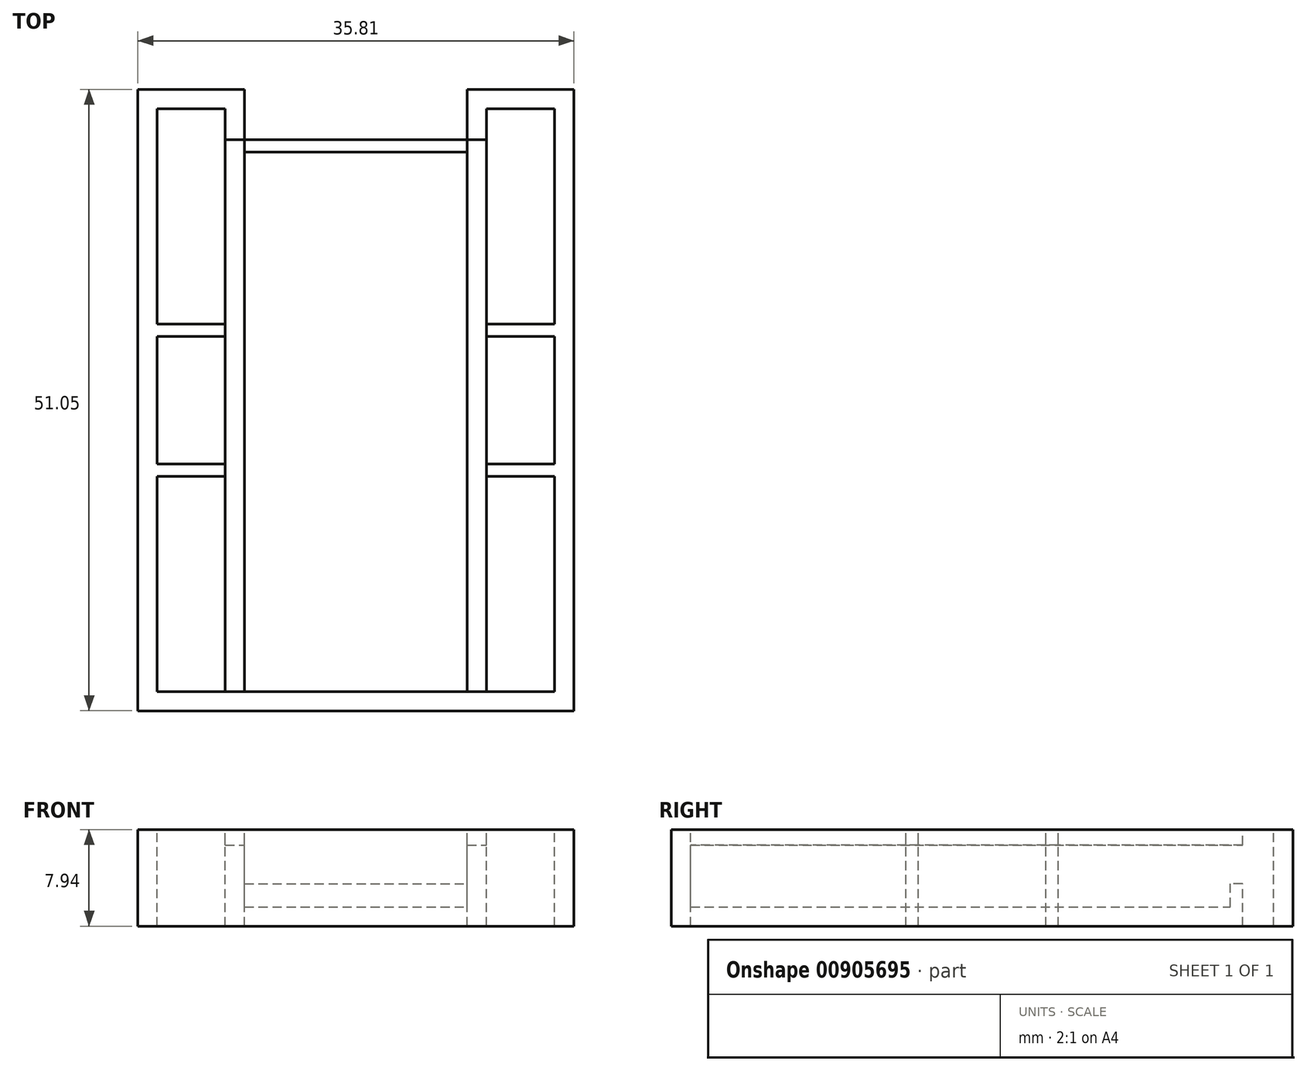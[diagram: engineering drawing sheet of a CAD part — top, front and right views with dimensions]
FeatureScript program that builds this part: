
annotation { "Feature Type Name" : "Feature", "Feature Type Description" : "" }
export const myFeature = defineFeature(function(context is Context, id is Id, definition is map)
    precondition{}
    {
        {
            var Q0;
            Q0=qCreatedBy(makeId("Top.planeOp"),FACE);
            var sketch = newSketch(context, id + "F0", { "sketchPlane" : qUnion([Q0])});
            skLineSegment(sketch, "E0.bottom", {"start": v(-17.05, 33.05) * mm, "end": v(18.76, 33.05) * mm});
            skLineSegment(sketch, "E0.top", {"start": v(-17.05, -18) * mm, "end": v(18.76, -18) * mm});
            skLineSegment(sketch, "E0.left", {"start": v(-17.05, 33.05) * mm, "end": v(-17.05, -18) * mm});
            skLineSegment(sketch, "E0.right", {"start": v(18.76, 33.05) * mm, "end": v(18.76, -18) * mm});
            skSolve(sketch);
        }
        {
            var Q0;
            Q0=makeQuery(id+"F0.imprint","IMPRINT",FACE,{"disambiguationData":[TD([[makeQuery(id+"F0.imprint","IMPRINT",EDGE,{"derivedFrom":sQuery(id+"F0.wireOp",EDGE,"E0.bottom")}),-1.0]])]});
            extrude(context, id + "F1", {"entities" : qUnion([Q0]), "depth" : 7.94 * mm, "offsetDistance" : 25.4 * mm});
        }
        {
            var Q0;
            Q0=makeQuery(id+"F1.opExtrude","CAP_FACE",FACE,{"disambiguationData":[OSD([sQuery(id+"F0.wireOp",EDGE,"E0.bottom"),sQuery(id+"F0.wireOp",EDGE,"E0.top"),sQuery(id+"F0.wireOp",EDGE,"E0.left"),sQuery(id+"F0.wireOp",EDGE,"E0.right")])],"isStart":false});
            var sketch = newSketch(context, id + "F2", { "sketchPlane" : qUnion([Q0])});
            skLineSegment(sketch, "E1.bottom", {"start": v(-15.47, 31.46) * mm, "end": v(-9.88, 31.46) * mm});
            skLineSegment(sketch, "E1.top", {"start": v(-15.47, 13.78) * mm, "end": v(-9.88, 13.78) * mm});
            skLineSegment(sketch, "E1.left", {"start": v(-15.47, 31.46) * mm, "end": v(-15.47, 13.78) * mm});
            skLineSegment(sketch, "E1.right", {"start": v(-9.88, 31.46) * mm, "end": v(-9.88, 13.78) * mm});
            skLineSegment(sketch, "E2.bottom", {"start": v(17.17, 31.46) * mm, "end": v(11.58, 31.46) * mm});
            skLineSegment(sketch, "E2.top", {"start": v(17.17, 13.78) * mm, "end": v(11.58, 13.78) * mm});
            skLineSegment(sketch, "E2.left", {"start": v(17.17, 31.46) * mm, "end": v(17.17, 13.78) * mm});
            skLineSegment(sketch, "E2.right", {"start": v(11.58, 31.46) * mm, "end": v(11.58, 13.78) * mm});
            skLineSegment(sketch, "E3.bottom", {"start": v(-15.47, 1.27) * mm, "end": v(-9.88, 1.27) * mm});
            skLineSegment(sketch, "E3.top", {"start": v(-15.47, -16.42) * mm, "end": v(-9.88, -16.42) * mm});
            skLineSegment(sketch, "E3.left", {"start": v(-15.47, 1.27) * mm, "end": v(-15.47, -16.42) * mm});
            skLineSegment(sketch, "E3.right", {"start": v(-9.88, 1.27) * mm, "end": v(-9.88, -16.42) * mm});
            skLineSegment(sketch, "E4.bottom", {"start": v(11.58, 1.27) * mm, "end": v(17.17, 1.27) * mm});
            skLineSegment(sketch, "E4.top", {"start": v(11.58, -16.42) * mm, "end": v(17.17, -16.42) * mm});
            skLineSegment(sketch, "E4.left", {"start": v(11.58, 1.27) * mm, "end": v(11.58, -16.42) * mm});
            skLineSegment(sketch, "E4.right", {"start": v(17.17, 1.27) * mm, "end": v(17.17, -16.42) * mm});
            skLineSegment(sketch, "E5.bottom", {"start": v(-15.47, 12.76) * mm, "end": v(-9.88, 12.76) * mm});
            skLineSegment(sketch, "E5.top", {"start": v(-15.47, 2.28) * mm, "end": v(-9.88, 2.28) * mm});
            skLineSegment(sketch, "E5.left", {"start": v(-15.47, 12.76) * mm, "end": v(-15.47, 2.28) * mm});
            skLineSegment(sketch, "E5.right", {"start": v(-9.88, 12.76) * mm, "end": v(-9.88, 2.28) * mm});
            skLineSegment(sketch, "E6.bottom", {"start": v(11.58, 12.76) * mm, "end": v(17.17, 12.76) * mm});
            skLineSegment(sketch, "E6.top", {"start": v(11.58, 2.28) * mm, "end": v(17.17, 2.28) * mm});
            skLineSegment(sketch, "E6.left", {"start": v(11.58, 12.76) * mm, "end": v(11.58, 2.28) * mm});
            skLineSegment(sketch, "E6.right", {"start": v(17.17, 12.76) * mm, "end": v(17.17, 2.28) * mm});
            skSolve(sketch);
        }
        {
            var Q0;
            Q0=makeQuery(id+"F2.imprint","IMPRINT",FACE,{"disambiguationData":[TD([[makeQuery(id+"F2.imprint","IMPRINT",EDGE,{"derivedFrom":sQuery(id+"F2.wireOp",EDGE,"E1.bottom")}),-1.0]])]});
            var Q1;
            Q1=makeQuery(id+"F2.imprint","IMPRINT",FACE,{"disambiguationData":[TD([[makeQuery(id+"F2.imprint","IMPRINT",EDGE,{"derivedFrom":sQuery(id+"F2.wireOp",EDGE,"E5.bottom")}),-1.0]])]});
            var Q2;
            Q2=makeQuery(id+"F2.imprint","IMPRINT",FACE,{"disambiguationData":[TD([[makeQuery(id+"F2.imprint","IMPRINT",EDGE,{"derivedFrom":sQuery(id+"F2.wireOp",EDGE,"E3.bottom")}),-1.0]])]});
            var Q3;
            Q3=makeQuery(id+"F2.imprint","IMPRINT",FACE,{"disambiguationData":[TD([[makeQuery(id+"F2.imprint","IMPRINT",EDGE,{"derivedFrom":sQuery(id+"F2.wireOp",EDGE,"E4.bottom")}),-1.0]])]});
            var Q4;
            Q4=makeQuery(id+"F2.imprint","IMPRINT",FACE,{"disambiguationData":[TD([[makeQuery(id+"F2.imprint","IMPRINT",EDGE,{"derivedFrom":sQuery(id+"F2.wireOp",EDGE,"E6.bottom")}),-1.0]])]});
            var Q5;
            Q5=makeQuery(id+"F2.imprint","IMPRINT",FACE,{"disambiguationData":[TD([[makeQuery(id+"F2.imprint","IMPRINT",EDGE,{"derivedFrom":sQuery(id+"F2.wireOp",EDGE,"E2.bottom")}),1.0]])]});
            extrude(context, id + "F3", {"entities" : qUnion([Q0, Q1, Q2, Q3, Q4, Q5]), "operationType" : NewBodyOperationType.REMOVE, "oppositeDirection" : true, "depth" : 25.4 * mm, "offsetDistance" : 25.4 * mm});
        }
        {
            var Q0;
            Q0=makeQuery(id+"F1.opExtrude","CAP_FACE",FACE,{"disambiguationData":[OSD([sQuery(id+"F0.wireOp",EDGE,"E0.bottom"),sQuery(id+"F0.wireOp",EDGE,"E0.top"),sQuery(id+"F0.wireOp",EDGE,"E0.left"),sQuery(id+"F0.wireOp",EDGE,"E0.right")])],"isStart":false});
            var sketch = newSketch(context, id + "F4", { "sketchPlane" : qUnion([Q0])});
            skLineSegment(sketch, "E7.bottom", {"start": v(-9.88, 28.92) * mm, "end": v(11.58, 28.92) * mm});
            skLineSegment(sketch, "E7.top", {"start": v(-9.88, -16.42) * mm, "end": v(11.58, -16.42) * mm});
            skLineSegment(sketch, "E7.left", {"start": v(-9.88, 28.92) * mm, "end": v(-9.88, -16.42) * mm});
            skLineSegment(sketch, "E7.right", {"start": v(11.58, 28.92) * mm, "end": v(11.58, -16.42) * mm});
            skSolve(sketch);
        }
        {
            var Q0;
            {var subQ8=sQuery(id+"F4.wireOp",EDGE,"E7.bottom");Q0=makeQuery(id+"F4.imprint","IMPRINT",FACE,{"disambiguationData":[TD([[makeQuery(id+"F4.imprint","IMPRINT",EDGE,{"derivedFrom":subQ8}),-1.0]])]});}
            extrude(context, id + "F5", {"entities" : qUnion([Q0]), "operationType" : NewBodyOperationType.REMOVE, "oppositeDirection" : true, "depth" : 1.27 * mm, "offsetDistance" : 25.4 * mm});
        }
        {
            var Q0;
            Q0=makeQuery(id+"F5.boolean.opBoolean","COPY",FACE,{"derivedFrom":makeQuery(id+"F5.opExtrude","CAP_FACE",FACE,{"disambiguationData":[OSD([sQuery(id+"F4.wireOp",EDGE,"E7.bottom"),sQuery(id+"F4.wireOp",EDGE,"E7.top"),sQuery(id+"F4.wireOp",EDGE,"E7.left"),sQuery(id+"F4.wireOp",EDGE,"E7.right")])],"isStart":false})});
            var sketch = newSketch(context, id + "F6", { "sketchPlane" : qUnion([Q0])});
            skLineSegment(sketch, "E8.bottom", {"start": v(-8.3, -16.42) * mm, "end": v(10, -16.42) * mm});
            skLineSegment(sketch, "E8.top", {"start": v(-8.3, 27.9) * mm, "end": v(10, 27.9) * mm});
            skLineSegment(sketch, "E8.left", {"start": v(-8.3, -16.42) * mm, "end": v(-8.3, 27.9) * mm});
            skLineSegment(sketch, "E8.right", {"start": v(10, -16.42) * mm, "end": v(10, 27.9) * mm});
            skSolve(sketch);
        }
        {
            var Q0;
            Q0=makeQuery(id+"F6.imprint","IMPRINT",FACE,{"disambiguationData":[TD([[makeQuery(id+"F6.imprint","IMPRINT",EDGE,{"derivedFrom":sQuery(id+"F6.wireOp",EDGE,"E8.bottom")}),1.0]])]});
            extrude(context, id + "F7", {"entities" : qUnion([Q0]), "operationType" : NewBodyOperationType.REMOVE, "oppositeDirection" : true, "depth" : 5.08 * mm, "offsetDistance" : 25.4 * mm});
        }
        {
            var Q0;
            Q0=makeQuery(id+"F1.opExtrude","CAP_FACE",FACE,{"disambiguationData":[OSD([sQuery(id+"F0.wireOp",EDGE,"E0.bottom"),sQuery(id+"F0.wireOp",EDGE,"E0.top"),sQuery(id+"F0.wireOp",EDGE,"E0.left"),sQuery(id+"F0.wireOp",EDGE,"E0.right")])],"isStart":false});
            var sketch = newSketch(context, id + "F8", { "sketchPlane" : qUnion([Q0])});
            skLineSegment(sketch, "E9.bottom", {"start": v(-8.3, 33.05) * mm, "end": v(10, 33.05) * mm});
            skLineSegment(sketch, "E9.top", {"start": v(-8.3, 28.92) * mm, "end": v(10, 28.92) * mm});
            skLineSegment(sketch, "E9.left", {"start": v(-8.3, 33.05) * mm, "end": v(-8.3, 28.92) * mm});
            skLineSegment(sketch, "E9.right", {"start": v(10, 33.05) * mm, "end": v(10, 28.92) * mm});
            skSolve(sketch);
        }
        {
            var Q0;
            Q0=makeQuery(id+"F8.imprint","IMPRINT",FACE,{"disambiguationData":[TD([[makeQuery(id+"F8.imprint","IMPRINT",EDGE,{"derivedFrom":sQuery(id+"F8.wireOp",EDGE,"E9.bottom")}),-1.0]])]});
            extrude(context, id + "F9", {"entities" : qUnion([Q0]), "operationType" : NewBodyOperationType.REMOVE, "oppositeDirection" : true, "depth" : 25.4 * mm, "offsetDistance" : 25.4 * mm});
        }
        {
            var Q0;
            Q0=makeQuery(id+"F5.boolean.opBoolean","COPY",FACE,{"derivedFrom":makeQuery(id+"F5.opExtrude","CAP_FACE",FACE,{"disambiguationData":[OSD([sQuery(id+"F4.wireOp",EDGE,"E7.bottom"),sQuery(id+"F4.wireOp",EDGE,"E7.top"),sQuery(id+"F4.wireOp",EDGE,"E7.left"),sQuery(id+"F4.wireOp",EDGE,"E7.right")])],"isStart":false})});
            var sketch = newSketch(context, id + "F10", { "sketchPlane" : qUnion([Q0])});
            skLineSegment(sketch, "E10.bottom", {"start": v(-8.3, 28.92) * mm, "end": v(10, 28.92) * mm});
            skLineSegment(sketch, "E10.top", {"start": v(-8.3, 27.9) * mm, "end": v(10, 27.9) * mm});
            skLineSegment(sketch, "E10.left", {"start": v(-8.3, 28.92) * mm, "end": v(-8.3, 27.9) * mm});
            skLineSegment(sketch, "E10.right", {"start": v(10, 28.92) * mm, "end": v(10, 27.9) * mm});
            skSolve(sketch);
        }
        {
            var Q0;
            Q0=makeQuery(id+"F10.imprint","IMPRINT",FACE,{"disambiguationData":[TD([[makeQuery(id+"F10.imprint","IMPRINT",EDGE,{"derivedFrom":sQuery(id+"F10.wireOp",EDGE,"E10.bottom")}),-1.0]])]});
            extrude(context, id + "F11", {"entities" : qUnion([Q0]), "operationType" : NewBodyOperationType.REMOVE, "oppositeDirection" : true, "depth" : 3.17 * mm, "offsetDistance" : 25.4 * mm});
        }
    });
